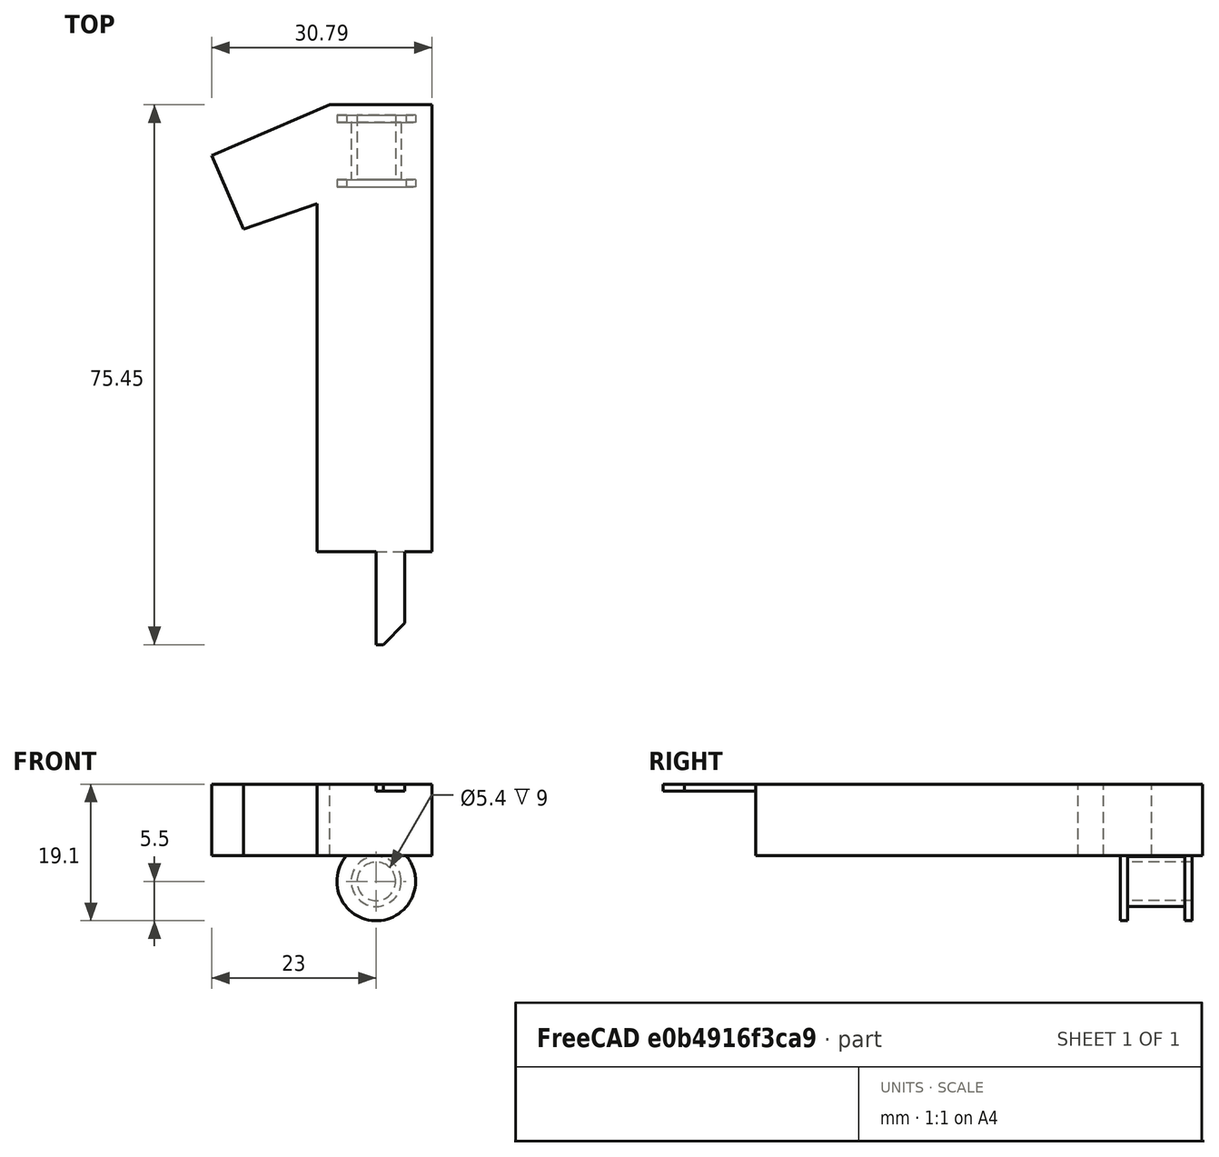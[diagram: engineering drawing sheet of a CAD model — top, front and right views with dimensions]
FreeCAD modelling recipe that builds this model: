
FCSTD DOCUMENT  (FreeCAD 0.17R12589 (Git))
Label: vela de cumpleaños
License: All rights reserved
LicenseURL: http://es.wikipedia.org/wiki/Todos_los_derechos_reservados
objects: Part::Cylinder×4, Part::MultiFuse×3, Part::Part2DObjectPython×1, Part::Extrusion×1, Part::Cut×1, Part::Box×1, Part::Chamfer×1
note: 12 computed .brp shape members not serialized (recipe doc carries the construction recipe); baked Part::Feature solids carry a one-line shape summary decoded from their .brp

FEATURE [Part::Part2DObjectPython] ShapeString  label="FORMA numero"  # Draft 2D object (typed FeaturePython)
  FontFile = <userpath>/Descargas/fonts (1)/Russo_One/RussoOne-Regular.ttf
  Size = 35
  String = 1
  Tracking = 0
FEATURE [Part::Extrusion] Extrude  label="numero"
  Base = -> ShapeString
  Dir = (0,0,1)
  DirMode = 2
  FaceMakerClass = Part::FaceMakerBullseye
  LengthFwd = 10
  LengthRev = 0
  Solid = true
  Symmetric = false
FEATURE [Part::Cylinder] Cylinder  label="Cilindro"
  Angle = 360
  AttacherType = Attacher::AttachEngine3D
  Height = 35
  Placement = pos=(23,87,-3) rot=(1,0,0;1.5708rad)
  Radius = 2.7
FEATURE [Part::Cylinder] Cylinder001  label="Cilindro001"
  Angle = 360
  AttacherType = Attacher::AttachEngine3D
  Height = 10
  Placement = pos=(23,61,-3) rot=(1,0,0;1.5708rad)
  Radius = 3.5
FEATURE [Part::Cylinder] Cylinder002  label="Cilindro002"
  Angle = 360
  AttacherType = Attacher::AttachEngine3D
  Height = 1
  Placement = pos=(23,61,-3) rot=(1,0,0;1.5708rad)
  Radius = 5.5
FEATURE [Part::Cylinder] Cylinder003  label="Cilindro003"
  Angle = 360
  AttacherType = Attacher::AttachEngine3D
  Height = 1
  Placement = pos=(23,52,-3) rot=(1,0,0;1.5708rad)
  Radius = 5.5
FEATURE [Part::MultiFuse] Fusion
  Shapes = -> [Cylinder001,Cylinder002,Cylinder003]
FEATURE [Part::Cut] Cut  label="soporte vela"
  Base = -> Fusion
  Placement = pos=(0,0,-0.6) rot=(0,0,1;0rad)
  Tool = -> Cylinder
FEATURE [Part::Box] Box  label="Cubo"
  AttacherType = Attacher::AttachEngine3D
  Height = 1
  Length = 4
  Placement = pos=(23,-13,9) rot=(0,0,1;0rad)
  Width = 15
FEATURE [Part::Chamfer] Chamfer  label="soporte a pastel"
  Base = -> Box
  Edges = 1 edges r=3: [Edge5]
FEATURE [Part::MultiFuse] Fusion001  label="numero completo"
  Shapes = -> [Chamfer,Extrude]
FEATURE [Part::MultiFuse] Fusion002  label="numero vela"
  Shapes = -> [Cut,Fusion001]
